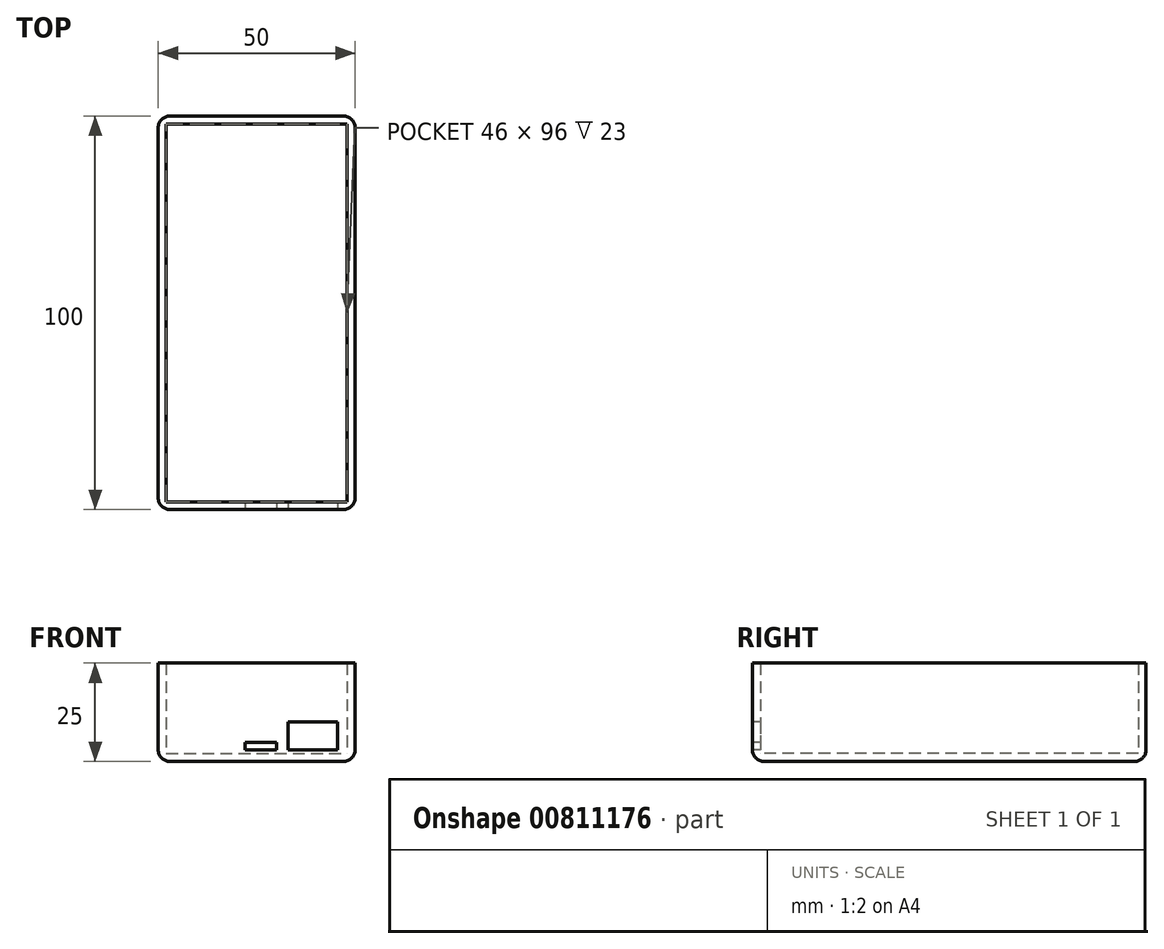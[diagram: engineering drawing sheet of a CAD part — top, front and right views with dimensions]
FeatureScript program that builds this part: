
annotation { "Feature Type Name" : "Feature", "Feature Type Description" : "" }
export const myFeature = defineFeature(function(context is Context, id is Id, definition is map)
    precondition{}
    {
        {
            var Q0;
            Q0=qCreatedBy(makeId("Top.planeOp"),FACE);
            var sketch = newSketch(context, id + "F0", { "sketchPlane" : qUnion([Q0])});
            skLineSegment(sketch, "E0.bottom", {"start": v(-25, 50) * mm, "end": v(25, 50) * mm});
            skLineSegment(sketch, "E0.top", {"start": v(-25, -50) * mm, "end": v(25, -50) * mm});
            skLineSegment(sketch, "E0.left", {"start": v(-25, 50) * mm, "end": v(-25, -50) * mm});
            skLineSegment(sketch, "E0.right", {"start": v(25, 50) * mm, "end": v(25, -50) * mm});
            skPoint(sketch, "E0.middle", {"position": v(0, 0) * mm});
            skSolve(sketch);
        }
        {
            var Q0;
            Q0=makeQuery(id+"F0.imprint","IMPRINT",FACE,{"disambiguationData":[TD([[makeQuery(id+"F0.imprint","IMPRINT",EDGE,{"derivedFrom":sQuery(id+"F0.wireOp",EDGE,"E0.bottom")}),-1.0]])]});
            extrude(context, id + "F1", {"entities" : qUnion([Q0]), "depth" : 25 * mm, "offsetDistance" : 25 * mm});
        }
        {
            var Q0;
            Q0=makeQuery(id+"F1.opExtrude","CAP_FACE",FACE,{"disambiguationData":[OSD([sQuery(id+"F0.wireOp",EDGE,"E0.bottom"),sQuery(id+"F0.wireOp",EDGE,"E0.top"),sQuery(id+"F0.wireOp",EDGE,"E0.left"),sQuery(id+"F0.wireOp",EDGE,"E0.right")])],"isStart":false});
            shell(context, id + "F2", {"entities" : qUnion([Q0]), "thickness" : 2 * mm});
        }
        {
            var Q0;
            Q0=makeQuery(id+"F1.opExtrude","SWEPT_FACE",FACE,{"disambiguationData":[OSD([sQuery(id+"F0.wireOp",EDGE,"E0.top")])]});
            var sketch = newSketch(context, id + "F3", { "sketchPlane" : qUnion([Q0])});
            skLineSegment(sketch, "E1", {"start": v(8, 10) * mm, "end": v(8, 3) * mm});
            skLineSegment(sketch, "E2", {"start": v(8, 3) * mm, "end": v(20.5, 3) * mm});
            skLineSegment(sketch, "E3", {"start": v(20.5, 3) * mm, "end": v(20.5, 10) * mm});
            skLineSegment(sketch, "E4", {"start": v(20.5, 10) * mm, "end": v(8, 10) * mm});
            skLineSegment(sketch, "E5", {"start": v(-3, 4.8) * mm, "end": v(-3, 3) * mm});
            skLineSegment(sketch, "E6", {"start": v(-3, 3) * mm, "end": v(5, 3) * mm});
            skLineSegment(sketch, "E7", {"start": v(5, 3) * mm, "end": v(5, 4.8) * mm});
            skLineSegment(sketch, "E8", {"start": v(5, 4.8) * mm, "end": v(-3, 4.8) * mm});
            skLineSegment(sketch, "E9", {"start": v(30.3, 11.6) * mm, "end": v(30.3, 10) * mm, "construction": true});
            skLineSegment(sketch, "E10", {"start": v(-18.6, 1.6) * mm, "end": v(-18.6, 0) * mm, "construction": true});
            skSolve(sketch);
        }
        {
            var Q0;
            Q0=makeQuery(id+"F3.imprint","IMPRINT",FACE,{"disambiguationData":[TD([[makeQuery(id+"F3.imprint","IMPRINT",EDGE,{"derivedFrom":sQuery(id+"F3.wireOp",EDGE,"E1")}),1.0]])]});
            var Q1;
            Q1=makeQuery(id+"F3.imprint","IMPRINT",FACE,{"disambiguationData":[TD([[makeQuery(id+"F3.imprint","IMPRINT",EDGE,{"derivedFrom":sQuery(id+"F3.wireOp",EDGE,"E5")}),1.0]])]});
            extrude(context, id + "F4", {"entities" : qUnion([Q0, Q1]), "operationType" : NewBodyOperationType.REMOVE, "oppositeDirection" : true, "depth" : 2 * mm, "offsetDistance" : 25 * mm});
        }
        {
            var Q0;
            Q0=makeQuery(id+"F1.opExtrude","SWEPT_EDGE",EDGE,{"disambiguationData":[OSD([sQuery(id+"F0.wireOp",EDGE,"E0.top"),sQuery(id+"F0.wireOp",EDGE,"E0.right")])]});
            fillet(context, id + "F5", {"entities" : qUnion([Q0]), "radius" : 3 * mm, "tangentPropagation" : true, "allowEdgeOverflow" : false});
        }
        {
            var Q0;
            Q0=makeQuery(id+"F1.opExtrude","SWEPT_EDGE",EDGE,{"disambiguationData":[OSD([sQuery(id+"F0.wireOp",EDGE,"E0.bottom"),sQuery(id+"F0.wireOp",EDGE,"E0.right")])]});
            var Q1;
            Q1=makeQuery(id+"F1.opExtrude","SWEPT_EDGE",EDGE,{"disambiguationData":[OSD([sQuery(id+"F0.wireOp",EDGE,"E0.bottom"),sQuery(id+"F0.wireOp",EDGE,"E0.left")])]});
            var Q2;
            Q2=makeQuery(id+"F1.opExtrude","SWEPT_EDGE",EDGE,{"disambiguationData":[OSD([sQuery(id+"F0.wireOp",EDGE,"E0.top"),sQuery(id+"F0.wireOp",EDGE,"E0.left")])]});
            var Q3;
            Q3=makeQuery(id+"F1.opExtrude","CAP_EDGE",EDGE,{"disambiguationData":[OSD([sQuery(id+"F0.wireOp",EDGE,"E0.left")])],"isStart":true});
            var Q4;
            Q4=makeQuery(id+"F1.opExtrude","CAP_EDGE",EDGE,{"disambiguationData":[OSD([sQuery(id+"F0.wireOp",EDGE,"E0.top")])],"isStart":true});
            var Q5;
            Q5=makeQuery(id+"F1.opExtrude","CAP_EDGE",EDGE,{"disambiguationData":[OSD([sQuery(id+"F0.wireOp",EDGE,"E0.bottom")])],"isStart":true});
            fillet(context, id + "F6", {"entities" : qUnion([Q0, Q1, Q2, Q3, Q4, Q5]), "radius" : 3 * mm, "tangentPropagation" : true, "allowEdgeOverflow" : false});
        }
    });
